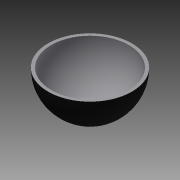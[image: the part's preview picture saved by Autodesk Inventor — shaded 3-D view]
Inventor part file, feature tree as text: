
AUTODESK INVENTOR PART (.ipt)
format: ipt  version: 2015 (Build 190159000, 159)  size: 140,800 bytes
history: native  units: in
note: dims shown in document units (in); Inventor stores cm internally (conversion verified against a paired STEP export)
features: sketch x2, revolve x1, plane x1, split x1, shell x1, other x1, extrude x1
ambient origin geometry x8: Origin, YZ Plane, XZ Plane, XY Plane, X Axis, Y Axis, Z Axis, Center Point
bodies: Solid1 (feature_tree)
feature tree (8):
  revolve  "Revolution1"  Angle=90.0deg
  plane  "Work Plane2"
  split  "Split2"
  shell  "Shell2"  Thickness=5.0in
  sketch  "Sketch1"  dims[d0=3.5in d1=90.0deg d5=5.0in d6=0.0in]
  sketch  "Sketch3"  dims[d7=0.125in]
  other  "Srf2"
  extrude  "ExtrusionSrf2"  [1 undecoded]
note: 1 required parameter value undecoded (feature->parameter linkage not recoverable at this tier; creation-order binding heuristic only, values carry confidence <= 0.55)
